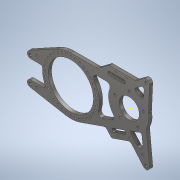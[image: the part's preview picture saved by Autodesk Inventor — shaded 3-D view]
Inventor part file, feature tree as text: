
AUTODESK INVENTOR PART (.ipt)
format: ipt  version: 2021 (Build 250183000, 183)  size: 571,904 bytes
history: native  units: in
note: dims shown in document units (in); Inventor stores cm internally (conversion verified against a paired STEP export)
features: sketch x21, extrude x16, hole x5, fillet x4, chamfer x1, projected_geometry x1
ambient origin geometry x8: Origin, YZ Plane, XZ Plane, XY Plane, X Axis, Y Axis, Z Axis, Center Point
bodies: Body1 (feature_tree)
feature tree (48):
  extrude  "Extrusion13"  Depth=0.5in TaperAngle=0.0deg
  hole  "Hole4"  [1 undecoded]
  extrude  "Extrusion15"  Depth=1.0in
  extrude  "Extrusion16"  Depth=0.5in TaperAngle=0.0deg
  hole  "Hole6"  [1 undecoded]
  extrude  "Extrusion17"  Depth=1.0in
  hole  "Hole7"  [1 undecoded]
  hole  "Hole9"  [1 undecoded]
  hole  "Hole10"  [1 undecoded]
  extrude  "Extrusion18"  Depth=1.0in
  extrude  "Extrusion19"  Depth=0.239in
  sketch  "Sketch33"  dims[d183=0.257in d184=0.75in d185=0.438in d186=0.25in d187=0.5635in d188=1.0in d189=0.8108in d191=1.0in]
  extrude  "Extrusion21"  Depth=0.5in
  extrude  "Extrusion22"  Depth=1.0in
  extrude  "Extrusion23"  Depth=0.75in
  extrude  "Extrusion24"  Depth=0.75in
  fillet  "Fillet2"  Radius=0.25in
  extrude  "Extrusion25"  Depth=1.0in TaperAngle=0.0deg
  extrude  "Extrusion26"  Depth=1.0in TaperAngle=0.0deg
  fillet  "Fillet3"  Radius=0.75in
  extrude  "Extrusion27"  Depth=0.75in
  chamfer  "Chamfer1"  Distance=0.25in
  sketch  "Sketch40"  dims[d211=0.75in d212=0.75in d213=0.25in]
  extrude  "Extrusion29"  Depth=1.0in TaperAngle=0.0deg
  extrude  "Extrusion30"  Depth=0.25in
  fillet  "Fillet4"  Radius=1.0in
  fillet  "Fillet5"  Radius=0.75in
  extrude  "Extrusion32"  Depth=1.0in TaperAngle=0.0deg
  sketch  "Sketch14"  dims[d96=8.5in d97=2.16in d98=9.0in d99=5.5in d100=1.0in d101=1.0in d102=6.0in d103=6.0in d104=3.718in d105=1.0in d108=10.718in d109=1.5in d111=0.5in d112=0.0in]
  sketch  "Sketch15"  dims[d113=0.386in d114=0.75in d115=0.762in d116=0.25in d117=0.5635in d118=0.484in d119=0.8108in d132=5.0in]
  sketch  "Sketch18"  dims[d133=17.223in d134=1.0in]
  sketch  "Sketch19"  dims[d135=1.0in d136=0.5in d137=0.0in]
  sketch  "Sketch20"  dims[d138=1.0in d140=4.0in]
  sketch  "Sketch21"  dims[d141=0.5in d142=0.0in d143=1.0in]
  sketch  "Sketch23"  dims[d144=1.625in]
  sketch  "Sketch27"  dims[d145=0.177in d146=0.75in d147=0.332in d148=0.25in d149=0.5635in d150=0.484in d151=0.8108in d155=1.0in d156=0.0in]
  sketch  "Sketch29"  dims[d157=1.625in]
  sketch  "Sketch31"  dims[d159=0.177in d160=0.75in d161=0.332in d162=0.25in d163=0.5635in d164=1.0in d165=0.8108in d178=7.75in]
  sketch  "Sketch32"  dims[d179=3.5433in d181=360.0deg]
  sketch  "Sketch34"  dims[d192=0.0481in d193=1.0in]
  sketch  "Sketch35"  dims[d194=0.3526in d197=0.239in]
  sketch  "Sketch36"  dims[d198=0.1195in d199=0.5in]
  sketch  "Sketch38"  dims[d200=0.266in d201=0.75in d202=0.507in d203=0.25in d204=0.5635in d205=1.0in d206=0.8108in d207=0.1718in]
  sketch  "Sketch39"  dims[d208=15.0deg d210=0.75in]
  sketch  "Sketch42"  dims[d214=0.5in d215=1.0in d216=0.0in]
  sketch  "Sketch43"  dims[d217=0.25in d218=1.0in d219=0.0in d220=0.75in]
  sketch  "Sketch45"  dims[d221=0.5in d223=0.75in d231=0.25in d232=1.0in d233=0.0in d234=0.25in d235=1.0in d236=0.0in d237=0.75in d238=1.0in d239=0.0in d242=1.0in d243=0.0in d244=0.25in d247=0.75in d249=0.75in d250=0.5in d251=2.8in d252=0.375in d253=1.25in d255=0.75in d256=0.75in d257=1.0in d258=0.0in d259=0.25in d260=1.0in d261=0.0in d262=0.25in d263=0.5in d264=1.0in d265=0.0in d266=0.0156in d267=0.125in d268=45.0deg d284=1.0in d285=0.0in d296=6.75in d297=1.0in d298=0.0in d303=3.005in d304=8.715in d305=6.5in d306=0.5in d307=0.5in d308=4.44in d309=0.325in d310=1.9685in d312=360.0deg d314=1.0in d315=0.0in d317=0.061in d283=0.5in d286=0.0344in]
  projected_geometry  "Project Cut Edges1"
note: 5 required parameter values undecoded (feature->parameter linkage not recoverable at this tier; creation-order binding heuristic only, values carry confidence <= 0.55)
